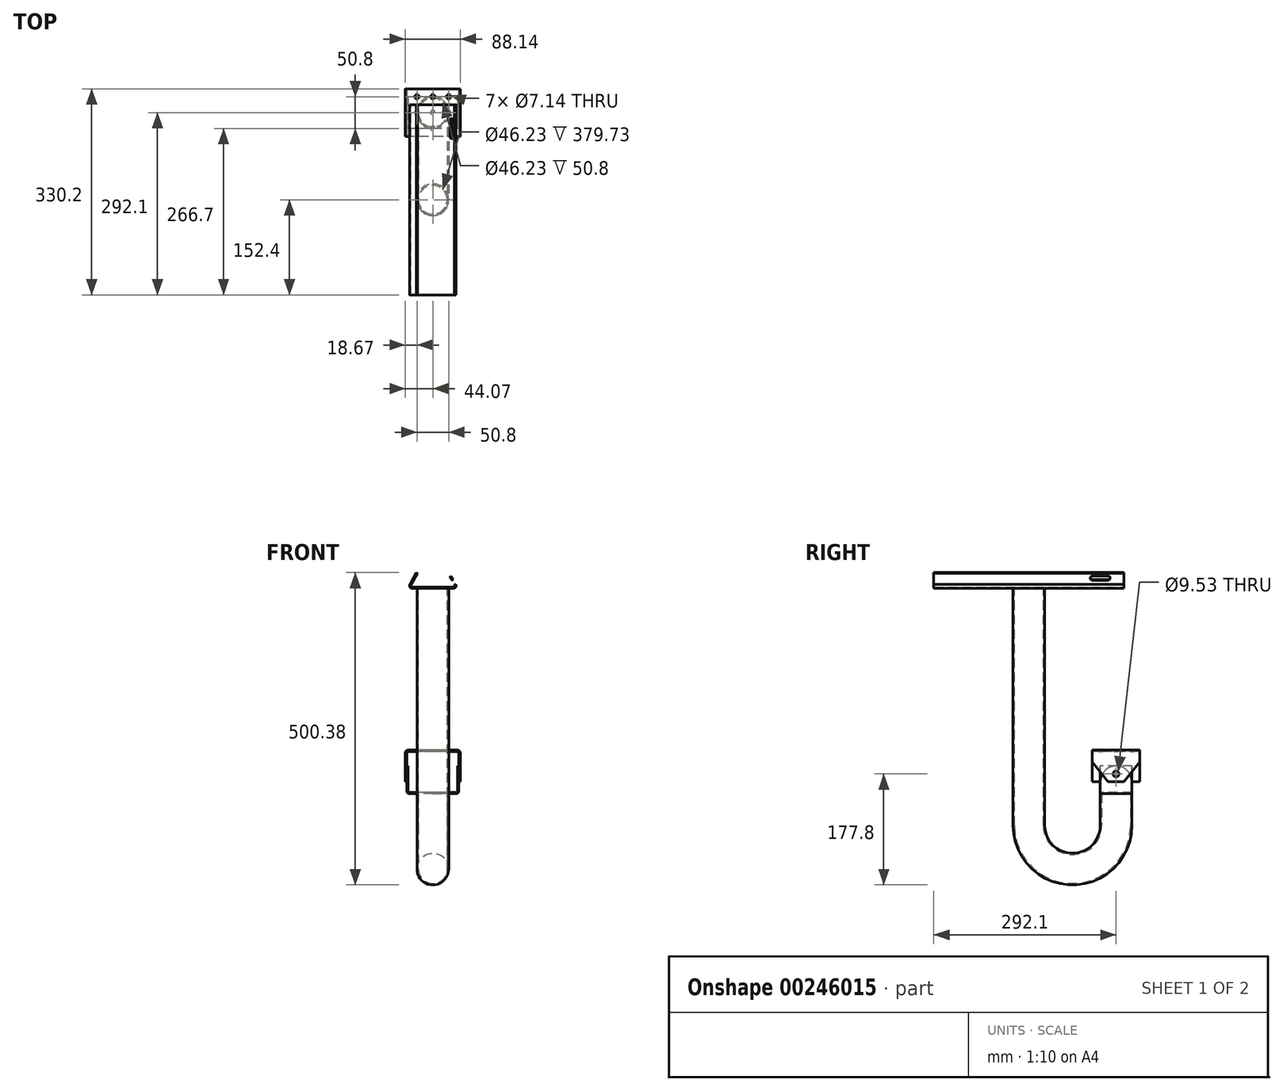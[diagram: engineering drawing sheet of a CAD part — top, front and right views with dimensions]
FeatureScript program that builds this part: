
annotation { "Feature Type Name" : "Feature", "Feature Type Description" : "" }
export const myFeature = defineFeature(function(context is Context, id is Id, definition is map)
    precondition{}
    {
        {
            var Q0;
            Q0=qCreatedBy(makeId("Front.planeOp"),FACE);
            var sketch = newSketch(context, id + "F0", { "sketchPlane" : qUnion([Q0])});
            skLineSegment(sketch, "E0", {"start": v(-32.86, 0) * mm, "end": v(32.86, 0) * mm});
            skLineSegment(sketch, "E1", {"start": v(36.81, 6.86) * mm, "end": v(26.1, 25.4) * mm});
            skLineSegment(sketch, "E2", {"start": v(-36.81, 6.86) * mm, "end": v(-26.1, 25.4) * mm});
            skLineSegment(sketch, "E3", {"start": v(0, 44.5) * mm, "end": v(0, -47.28) * mm, "construction": true});
            skLineSegment(sketch, "E4.0", {"start": v(-32.86, 2.29) * mm, "end": v(32.86, 2.29) * mm});
            skLineSegment(sketch, "E5.0", {"start": v(-34.84, 5.71) * mm, "end": v(-24.13, 24.26) * mm});
            skLineSegment(sketch, "E6.0", {"start": v(34.84, 5.71) * mm, "end": v(24.13, 24.26) * mm});
            skLineSegment(sketch, "E7", {"start": v(-26.1, 25.4) * mm, "end": v(-24.13, 24.26) * mm});
            skLineSegment(sketch, "E8", {"start": v(24.13, 24.26) * mm, "end": v(26.1, 25.4) * mm});
            skPoint(sketch, "E9.visualSharp", {"position": v(-36.81, 2.29) * mm});
            skArc(sketch, "E9.filletArc", {"start": v(-34.84, 5.72) * mm, "mid": v(-34.84, 3.43) * mm, "end": v(-32.86, 2.29) * mm});
            skPoint(sketch, "E10.visualSharp", {"position": v(36.81, 2.29) * mm});
            skArc(sketch, "E10.filletArc", {"start": v(32.86, 2.29) * mm, "mid": v(34.84, 3.43) * mm, "end": v(34.84, 5.72) * mm});
            skPoint(sketch, "E11.visualSharp", {"position": v(-40.77, 0) * mm});
            skArc(sketch, "E11.filletArc", {"start": v(-36.81, 6.86) * mm, "mid": v(-36.81, 2.29) * mm, "end": v(-32.86, 0) * mm});
            skPoint(sketch, "E12.visualSharp", {"position": v(40.77, 0) * mm});
            skArc(sketch, "E12.filletArc", {"start": v(32.86, 0) * mm, "mid": v(36.81, 2.29) * mm, "end": v(36.81, 6.86) * mm});
            skSolve(sketch);
        }
        {
            var Q0;
            Q0=makeQuery(id+"F0.imprint","IMPRINT",FACE,{"disambiguationData":[TD([[makeQuery(id+"F0.imprint","IMPRINT",EDGE,{"derivedFrom":sQuery(id+"F0.wireOp",EDGE,"E0")}),1.0]])]});
            extrude(context, id + "F1", {"entities" : qUnion([Q0]), "depth" : 304.8 * mm});
        }
        {
            var Q0;
            Q0=makeQuery(id+"F1.opExtrude","CAP_FACE",FACE,{"disambiguationData":[OSD([sQuery(id+"F0.wireOp",EDGE,"E0"),sQuery(id+"F0.wireOp",EDGE,"E1"),sQuery(id+"F0.wireOp",EDGE,"E2"),sQuery(id+"F0.wireOp",EDGE,"E4.0"),sQuery(id+"F0.wireOp",EDGE,"E5.0"),sQuery(id+"F0.wireOp",EDGE,"E6.0"),sQuery(id+"F0.wireOp",EDGE,"E7"),sQuery(id+"F0.wireOp",EDGE,"E8"),sQuery(id+"F0.wireOp",EDGE,"E9.filletArc"),sQuery(id+"F0.wireOp",EDGE,"E10.filletArc"),sQuery(id+"F0.wireOp",EDGE,"E11.filletArc"),sQuery(id+"F0.wireOp",EDGE,"E12.filletArc")])],"isStart":false});
            cPlane(context, id + "F2", {"entities" : qUnion([Q0]), "cplaneType" : CPlaneType.OFFSET, "offset" : 152.4 * mm, "oppositeDirection" : true, "width" : 152.4 * mm, "height" : 152.4 * mm});
        }
        {
            var Q0;
            Q0=qCreatedBy(makeId("Right.planeOp"),FACE);
            var sketch = newSketch(context, id + "F3", { "sketchPlane" : qUnion([Q0])});
            skLineSegment(sketch, "E13", {"start": v(-152.4, 0) * mm, "end": v(-152.4, -379.73) * mm});
            skLineSegment(sketch, "E14.0", {"start": v(-304.8, -449.58) * mm, "end": v(0, -449.58) * mm, "construction": true});
            skLineSegment(sketch, "E15.0", {"start": v(-12.7, -259.08) * mm, "end": v(-12.7, -379.73) * mm});
            skArc(sketch, "E16", {"start": v(-152.4, -379.73) * mm, "mid": v(-82.55, -449.58) * mm, "end": v(-12.7, -379.73) * mm});
            skPoint(sketch, "E16.first.point", {"position": v(-152.4, -379.73) * mm});
            skPoint(sketch, "E16.second.point", {"position": v(-12.7, -379.73) * mm});
            skPoint(sketch, "E16.third.point", {"position": v(-82.55, -449.58) * mm});
            skSolve(sketch);
        }
        {
            var Q0;
            Q0=sQuery(id+"F3.wireOp",VERTEX,"E15.0.start");
            var Q1;
            Q1=qCreatedBy(makeId("Top.planeOp"),FACE);
            cPlane(context, id + "F4", {"entities" : qUnion([Q0, Q1]), "cplaneType" : CPlaneType.PLANE_POINT, "offset" : 25.4 * mm, "width" : 152.4 * mm, "height" : 152.4 * mm});
        }
        {
            var Q0;
            Q0=qCreatedBy(id+"F4.planeOp",FACE);
            var sketch = newSketch(context, id + "F5", { "sketchPlane" : qUnion([Q0])});
            skCircle(sketch, "E17", {"center": v(0, -12.7) * mm, "radius": 25.4 * mm});
            skCircle(sketch, "E18", {"center": v(0, -12.7) * mm, "radius": 23.11 * mm});
            skSolve(sketch);
        }
        {
            var Q0;
            Q0 = qSketchRegion(id + "F5", true);
            var Q1;
            Q1 = qConstructionFilter(qBodyType(qCreatedBy(id + "F3" ,EDGE), BodyType.WIRE), ConstructionObject.NO);
            sweep(context, id + "F6", {"operationType" : NewBodyOperationType.ADD, "profiles" : qUnion([Q0]), "path" : qUnion([Q1])});
        }
        {
            var Q0;
            Q0=sQuery(id+"F3.wireOp",EDGE,"E15.0");
            var Q1;
            Q1=qCreatedBy(makeId("Front.planeOp"),FACE);
            cPlane(context, id + "F7", {"entities" : qUnion([Q0, Q1]), "cplaneType" : CPlaneType.LINE_ANGLE, "offset" : 25.4 * mm, "angle" : 0 * degree, "width" : 152.4 * mm, "height" : 152.4 * mm});
        }
        {
            var Q0;
            Q0=qCreatedBy(id+"F7.planeOp",FACE);
            var sketch = newSketch(context, id + "F8", { "sketchPlane" : qUnion([Q0])});
            skLineSegment(sketch, "E19", {"start": v(-44.07, -309.88) * mm, "end": v(-44.07, -263.65) * mm});
            skLineSegment(sketch, "E20", {"start": v(-39.5, -259.08) * mm, "end": v(39.5, -259.08) * mm});
            skLineSegment(sketch, "E21", {"start": v(44.07, -263.65) * mm, "end": v(44.07, -309.88) * mm});
            skLineSegment(sketch, "E22.0", {"start": v(41.78, -263.65) * mm, "end": v(41.78, -309.88) * mm});
            skLineSegment(sketch, "E22.1", {"start": v(-39.5, -261.37) * mm, "end": v(39.5, -261.37) * mm});
            skLineSegment(sketch, "E22.2", {"start": v(-41.78, -309.88) * mm, "end": v(-41.78, -263.65) * mm});
            skLineSegment(sketch, "E23", {"start": v(-41.78, -309.88) * mm, "end": v(-44.07, -309.88) * mm});
            skLineSegment(sketch, "E24", {"start": v(41.78, -309.88) * mm, "end": v(44.07, -309.88) * mm});
            skLineSegment(sketch, "E25", {"start": v(0, -226.25) * mm, "end": v(0, -315.7) * mm, "construction": true});
            skPoint(sketch, "E26.visualSharp", {"position": v(-41.78, -261.37) * mm});
            skArc(sketch, "E26.filletArc", {"start": v(-39.5, -261.37) * mm, "mid": v(-41.11, -262.04) * mm, "end": v(-41.78, -263.65) * mm});
            skPoint(sketch, "E27.visualSharp", {"position": v(41.78, -261.37) * mm});
            skArc(sketch, "E27.filletArc", {"start": v(41.78, -263.65) * mm, "mid": v(41.11, -262.04) * mm, "end": v(39.5, -261.37) * mm});
            skPoint(sketch, "E28.visualSharp", {"position": v(-44.07, -259.08) * mm});
            skArc(sketch, "E28.filletArc", {"start": v(-39.5, -259.08) * mm, "mid": v(-42.73, -260.42) * mm, "end": v(-44.07, -263.65) * mm});
            skPoint(sketch, "E29.visualSharp", {"position": v(44.07, -259.08) * mm});
            skArc(sketch, "E29.filletArc", {"start": v(44.07, -263.65) * mm, "mid": v(42.73, -260.42) * mm, "end": v(39.5, -259.08) * mm});
            skSolve(sketch);
        }
        {
            var Q0;
            Q0 = qSketchRegion(id + "F8", true);
            extrude(context, id + "F9", {"entities" : qUnion([Q0]), "operationType" : NewBodyOperationType.ADD, "endBound" : BoundingType.SYMMETRIC, "depth" : 76.2 * mm});
        }
        {
            var Q0;
            Q0=makeQuery(id+"F9.opExtrude","SWEPT_FACE",FACE,{"disambiguationData":[OSD([sQuery(id+"F8.wireOp",EDGE,"E19")])]});
            var sketch = newSketch(context, id + "F10", { "sketchPlane" : qUnion([Q0])});
            skLineSegment(sketch, "E30", {"start": v(-50.8, -278.13) * mm, "end": v(-25.4, -309.88) * mm});
            skLineSegment(sketch, "E31", {"start": v(-25.4, -309.88) * mm, "end": v(-50.8, -309.88) * mm});
            skLineSegment(sketch, "E32", {"start": v(-50.8, -309.88) * mm, "end": v(-50.8, -278.13) * mm});
            skLineSegment(sketch, "E33", {"start": v(-12.7, -246.82) * mm, "end": v(-12.7, -322.13) * mm, "construction": true});
            skLineSegment(sketch, "E34.MirrorCS", {"start": v(25.4, -309.88) * mm, "end": v(25.4, -278.13) * mm});
            skLineSegment(sketch, "E35.MirrorCS", {"start": v(25.4, -278.13) * mm, "end": v(0, -309.88) * mm});
            skLineSegment(sketch, "E36.MirrorCS", {"start": v(0, -309.88) * mm, "end": v(25.4, -309.88) * mm});
            skCircle(sketch, "E37", {"center": v(-12.7, -297.18) * mm, "radius": 4.76 * mm});
            skSolve(sketch);
        }
        {
            var Q0;
            Q0=makeQuery(id+"F10.imprint","IMPRINT",FACE,{"disambiguationData":[TD([[makeQuery(id+"F10.imprint","IMPRINT",EDGE,{"derivedFrom":sQuery(id+"F10.wireOp",EDGE,"E30")}),-1.0]])]});
            var Q1;
            Q1=makeQuery(id+"F10.imprint","IMPRINT",FACE,{"disambiguationData":[TD([[makeQuery(id+"F10.imprint","IMPRINT",EDGE,{"derivedFrom":sQuery(id+"F10.wireOp",EDGE,"E34.MirrorCS")}),1.0]])]});
            var Q2;
            Q2=makeQuery(id+"F10.imprint","IMPRINT",FACE,{"disambiguationData":[TD([[makeQuery(id+"F10.imprint","IMPRINT",EDGE,{"derivedFrom":sQuery(id+"F10.wireOp",EDGE,"E37")}),1.0]])]});
            extrude(context, id + "F11", {"entities" : qUnion([Q0, Q1, Q2]), "operationType" : NewBodyOperationType.REMOVE, "endBound" : BoundingType.UP_TO_NEXT, "oppositeDirection" : true, "depth" : 25.4 * mm});
        }
        {
            var Q0;
            Q0=makeQuery(id+"F9.boolean.opBoolean","MERGE",FACE,{"derivedFrom":[makeQuery(id+"F6.opSweep","CAP_FACE",FACE,{"disambiguationData":[OSD([sQuery(id+"F3.wireOp",VERTEX,"E15.0.start"),sQuery(id+"F5.wireOp",EDGE,"E17"),sQuery(id+"F5.wireOp",EDGE,"E18")])],"isStart":true}),makeQuery(id+"F9.opExtrude","SWEPT_FACE",FACE,{"disambiguationData":[OSD([sQuery(id+"F8.wireOp",EDGE,"E20")])]})]});
            var sketch = newSketch(context, id + "F12", { "sketchPlane" : qUnion([Q0])});
            skPoint(sketch, "E38", {"position": v(0, -12.7) * mm});
            skPoint(sketch, "E39", {"position": v(25.4, -12.7) * mm});
            skPoint(sketch, "E40", {"position": v(-25.4, -12.7) * mm});
            skPoint(sketch, "E41", {"position": v(-25.4, 12.7) * mm});
            skPoint(sketch, "E42", {"position": v(0, 12.7) * mm});
            skPoint(sketch, "E43", {"position": v(25.4, 12.7) * mm});
            skPoint(sketch, "E44", {"position": v(0, -38.1) * mm});
            skSolve(sketch);
        }
        {
            var Q0;
            Q0=sQuery(id+"F12.wireOp",VERTEX,"E44");
            var Q1;
            Q1=sQuery(id+"F12.wireOp",VERTEX,"E38");
            var Q2;
            Q2=sQuery(id+"F12.wireOp",VERTEX,"E40");
            var Q3;
            Q3=sQuery(id+"F12.wireOp",VERTEX,"E41");
            var Q4;
            Q4=sQuery(id+"F12.wireOp",VERTEX,"E42");
            var Q5;
            Q5=sQuery(id+"F12.wireOp",VERTEX,"E43");
            var Q6;
            Q6=sQuery(id+"F12.wireOp",VERTEX,"E39");
            var Q7;
            Q7=makeQuery(id+"F1.opExtrude","SWEPT_BODY",BODY,{"disambiguationData":[OSD([sQuery(id+"F0.wireOp",EDGE,"E0"),sQuery(id+"F0.wireOp",EDGE,"E1"),sQuery(id+"F0.wireOp",EDGE,"E2"),sQuery(id+"F0.wireOp",EDGE,"E4.0"),sQuery(id+"F0.wireOp",EDGE,"E5.0"),sQuery(id+"F0.wireOp",EDGE,"E6.0"),sQuery(id+"F0.wireOp",EDGE,"E7"),sQuery(id+"F0.wireOp",EDGE,"E8"),sQuery(id+"F0.wireOp",EDGE,"E9.filletArc"),sQuery(id+"F0.wireOp",EDGE,"E10.filletArc"),sQuery(id+"F0.wireOp",EDGE,"E11.filletArc"),sQuery(id+"F0.wireOp",EDGE,"E12.filletArc")])]});
            hole(context, id + "F13", {"style" : HoleStyle.SIMPLE, "endStyle" : HoleEndStyle.BLIND, "holeDiameter" : 7.14 * mm, "holeDepth" : 2.3 * mm, "tappedDepth" : 12.7 * mm, "tapClearance" : 3, "locations" : qUnion([Q0, Q1, Q2, Q3, Q4, Q5, Q6]), "scope" : qUnion([Q7])});
        }
        {
            var Q0;
            Q0=qCreatedBy(id+"F4.planeOp",FACE);
            cPlane(context, id + "F14", {"entities" : qUnion([Q0]), "cplaneType" : CPlaneType.OFFSET, "offset" : 69.85 * mm, "oppositeDirection" : true, "width" : 152.4 * mm, "height" : 152.4 * mm});
        }
        {
            var Q0;
            Q0=qCreatedBy(id+"F7.planeOp",FACE);
            var sketch = newSketch(context, id + "F15", { "sketchPlane" : qUnion([Q0])});
            skLineSegment(sketch, "E45", {"start": v(-37.21, -328.93) * mm, "end": v(37.21, -328.93) * mm});
            skLineSegment(sketch, "E46", {"start": v(-41.78, -324.36) * mm, "end": v(-41.78, -284.48) * mm});
            skLineSegment(sketch, "E47", {"start": v(-41.78, -284.48) * mm, "end": v(-39.5, -284.48) * mm});
            skLineSegment(sketch, "E48", {"start": v(-39.5, -284.48) * mm, "end": v(-39.5, -324.36) * mm});
            skLineSegment(sketch, "E49", {"start": v(-37.21, -326.64) * mm, "end": v(37.21, -326.64) * mm});
            skLineSegment(sketch, "E50", {"start": v(39.5, -324.36) * mm, "end": v(39.5, -284.48) * mm});
            skLineSegment(sketch, "E51", {"start": v(39.5, -284.48) * mm, "end": v(41.78, -284.48) * mm});
            skLineSegment(sketch, "E52", {"start": v(41.78, -284.48) * mm, "end": v(41.78, -324.36) * mm});
            skPoint(sketch, "E53.visualSharp", {"position": v(-39.5, -326.64) * mm});
            skArc(sketch, "E53.filletArc", {"start": v(-39.5, -324.36) * mm, "mid": v(-38.83, -325.97) * mm, "end": v(-37.21, -326.64) * mm});
            skPoint(sketch, "E54.visualSharp", {"position": v(39.5, -326.64) * mm});
            skArc(sketch, "E54.filletArc", {"start": v(37.21, -326.64) * mm, "mid": v(38.83, -325.97) * mm, "end": v(39.5, -324.36) * mm});
            skPoint(sketch, "E55.visualSharp", {"position": v(-41.78, -328.93) * mm});
            skArc(sketch, "E55.filletArc", {"start": v(-41.78, -324.36) * mm, "mid": v(-40.44, -327.6) * mm, "end": v(-37.21, -328.93) * mm});
            skPoint(sketch, "E56.visualSharp", {"position": v(41.78, -328.93) * mm});
            skArc(sketch, "E56.filletArc", {"start": v(37.21, -328.93) * mm, "mid": v(40.44, -327.6) * mm, "end": v(41.78, -324.36) * mm});
            skSolve(sketch);
        }
        {
            var Q0;
            Q0=makeQuery(id+"F15.imprint","IMPRINT",FACE,{"disambiguationData":[TD([[makeQuery(id+"F15.imprint","IMPRINT",EDGE,{"derivedFrom":sQuery(id+"F15.wireOp",EDGE,"E45")}),1.0]])]});
            extrude(context, id + "F16", {"entities" : qUnion([Q0]), "operationType" : NewBodyOperationType.ADD, "depth" : 25.4 * mm, "hasSecondDirection" : true, "secondDirectionOppositeDirection" : true, "secondDirectionDepth" : 25.4 * mm});
        }
        {
            var Q0;
            Q0=makeQuery(id+"F16.opExtrude","SWEPT_FACE",FACE,{"disambiguationData":[OSD([sQuery(id+"F15.wireOp",EDGE,"E48")])]});
            var sketch = newSketch(context, id + "F17", { "sketchPlane" : qUnion([Q0])});
            skArc(sketch, "E57", {"start": v(38.1, -309.88) * mm, "mid": v(12.7, -284.48) * mm, "end": v(-12.7, -309.88) * mm});
            skLineSegment(sketch, "E58", {"start": v(38.1, -309.88) * mm, "end": v(38.1, -284.48) * mm});
            skLineSegment(sketch, "E59", {"start": v(38.1, -284.48) * mm, "end": v(-12.7, -284.48) * mm});
            skLineSegment(sketch, "E60", {"start": v(-12.7, -284.48) * mm, "end": v(-12.7, -309.88) * mm});
            skCircle(sketch, "E61", {"center": v(12.7, -297.18) * mm, "radius": 4.76 * mm});
            skSolve(sketch);
        }
        {
            var Q0;
            {var subQ0=sQuery(id+"F17.wireOp",EDGE,"E60");Q0=makeQuery(id+"F17.imprint","IMPRINT",FACE,{"disambiguationData":[TD([[makeQuery(id+"F17.imprint","IMPRINT",EDGE,{"derivedFrom":subQ0}),1.0]])]});}
            var Q1;
            {var subQ0=sQuery(id+"F17.wireOp",EDGE,"E58");Q1=makeQuery(id+"F17.imprint","IMPRINT",FACE,{"disambiguationData":[TD([[makeQuery(id+"F17.imprint","IMPRINT",EDGE,{"derivedFrom":subQ0}),-1.0]])]});}
            var Q2;
            Q2=makeQuery(id+"F17.imprint","IMPRINT",FACE,{"disambiguationData":[TD([[makeQuery(id+"F17.imprint","IMPRINT",EDGE,{"derivedFrom":sQuery(id+"F17.wireOp",EDGE,"E61")}),1.0]])]});
            extrude(context, id + "F18", {"entities" : qUnion([Q0, Q1, Q2]), "operationType" : NewBodyOperationType.REMOVE, "oppositeDirection" : true, "depth" : 2.3 * mm});
        }
        {
            var Q0;
            Q0=qCreatedBy(id+"F7.planeOp",FACE);
            var sketch = newSketch(context, id + "F19", { "sketchPlane" : qUnion([Q0])});
            skLineSegment(sketch, "E62.bottom", {"start": v(-31.75, -326.64) * mm, "end": v(31.75, -326.64) * mm});
            skLineSegment(sketch, "E62.top", {"start": v(-31.75, -261.37) * mm, "end": v(31.75, -261.37) * mm});
            skLineSegment(sketch, "E62.left", {"start": v(-31.75, -326.64) * mm, "end": v(-31.75, -261.37) * mm});
            skLineSegment(sketch, "E62.right", {"start": v(31.75, -326.64) * mm, "end": v(31.75, -261.37) * mm});
            skSolve(sketch);
        }
        {
            var Q0;
            Q0=makeQuery(id+"F19.imprint","IMPRINT",FACE,{"disambiguationData":[TD([[makeQuery(id+"F19.imprint","IMPRINT",EDGE,{"derivedFrom":sQuery(id+"F19.wireOp",EDGE,"E62.bottom")}),1.0]])]});
            extrude(context, id + "F20", {"entities" : qUnion([Q0]), "operationType" : NewBodyOperationType.REMOVE, "oppositeDirection" : true, "depth" : 31.75 * mm, "hasSecondDirection" : true, "secondDirectionOppositeDirection" : false, "secondDirectionDepth" : 31.75 * mm});
        }
        {
            var Q0;
            Q0=makeQuery(id+"F1.opExtrude","SWEPT_FACE",FACE,{"disambiguationData":[OSD([sQuery(id+"F0.wireOp",EDGE,"E1")])]});
            var sketch = newSketch(context, id + "F21", { "sketchPlane" : qUnion([Q0])});
            skArc(sketch, "E63", {"start": v(-279.4, 2.6) * mm, "mid": v(-282.58, -0.58) * mm, "end": v(-279.4, -3.76) * mm});
            skArc(sketch, "E64", {"start": v(-254, -3.76) * mm, "mid": v(-250.83, -0.58) * mm, "end": v(-254, 2.6) * mm});
            skLineSegment(sketch, "E65", {"start": v(-279.4, 2.6) * mm, "end": v(-254, 2.6) * mm});
            skLineSegment(sketch, "E66", {"start": v(-279.4, -3.76) * mm, "end": v(-254, -3.76) * mm});
            skLineSegment(sketch, "E67", {"start": v(-152.4, 93.04) * mm, "end": v(-152.4, -99.81) * mm, "construction": true});
            skPoint(sketch, "E67.startSnap0", {"position": v(-152.4, -12.47) * mm});
            skArc(sketch, "E68.MirrorCS", {"start": v(-25.4, 2.6) * mm, "mid": v(-22.23, -0.58) * mm, "end": v(-25.4, -3.76) * mm});
            skLineSegment(sketch, "E69.MirrorCS", {"start": v(-25.4, 2.6) * mm, "end": v(-50.8, 2.6) * mm});
            skArc(sketch, "E70.MirrorCS", {"start": v(-50.8, -3.76) * mm, "mid": v(-53.98, -0.58) * mm, "end": v(-50.8, 2.6) * mm});
            skLineSegment(sketch, "E71.MirrorCS", {"start": v(-25.4, -3.76) * mm, "end": v(-50.8, -3.76) * mm});
            skArc(sketch, "E72", {"start": v(-165.1, 2.6) * mm, "mid": v(-168.28, -0.58) * mm, "end": v(-165.1, -3.76) * mm});
            skArc(sketch, "E73", {"start": v(-139.7, -3.76) * mm, "mid": v(-136.53, -0.58) * mm, "end": v(-139.7, 2.6) * mm});
            skLineSegment(sketch, "E74", {"start": v(-165.1, 2.6) * mm, "end": v(-139.7, 2.6) * mm});
            skLineSegment(sketch, "E75", {"start": v(-165.1, -3.76) * mm, "end": v(-139.7, -3.76) * mm});
            skSolve(sketch);
        }
        {
            var Q0;
            Q0=makeQuery(id+"F21.imprint","IMPRINT",FACE,{"disambiguationData":[TD([[makeQuery(id+"F21.imprint","IMPRINT",EDGE,{"derivedFrom":sQuery(id+"F21.wireOp",EDGE,"E63")}),1.0]])]});
            var Q1;
            Q1=makeQuery(id+"F21.imprint","IMPRINT",FACE,{"disambiguationData":[TD([[makeQuery(id+"F21.imprint","IMPRINT",EDGE,{"derivedFrom":sQuery(id+"F21.wireOp",EDGE,"E72")}),1.0]])]});
            var Q2;
            Q2=makeQuery(id+"F21.imprint","IMPRINT",FACE,{"disambiguationData":[TD([[makeQuery(id+"F21.imprint","IMPRINT",EDGE,{"derivedFrom":sQuery(id+"F21.wireOp",EDGE,"E68.MirrorCS")}),-1.0]])]});
            extrude(context, id + "F22", {"entities" : qUnion([Q0, Q1, Q2]), "operationType" : NewBodyOperationType.REMOVE, "endBound" : BoundingType.UP_TO_NEXT, "oppositeDirection" : true, "depth" : 25.4 * mm});
        }
    });
